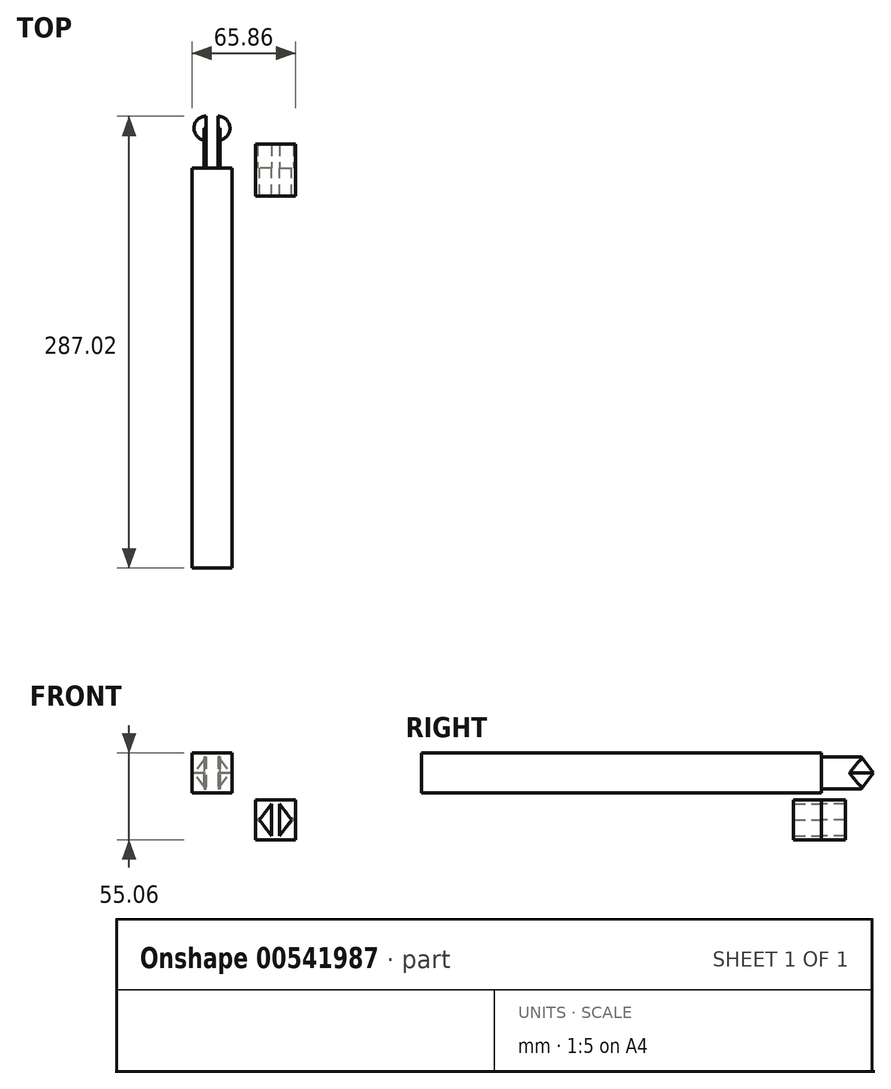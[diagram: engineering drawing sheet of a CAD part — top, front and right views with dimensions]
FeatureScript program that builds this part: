
annotation { "Feature Type Name" : "Feature", "Feature Type Description" : "" }
export const myFeature = defineFeature(function(context is Context, id is Id, definition is map)
    precondition{}
    {
        {
            var Q0;
            Q0=qCreatedBy(makeId("Front.planeOp"),FACE);
            var sketch = newSketch(context, id + "F0", { "sketchPlane" : qUnion([Q0])});
            skLineSegment(sketch, "E0.bottom", {"start": v(-53.16, 42.36) * mm, "end": v(-27.76, 42.36) * mm});
            skLineSegment(sketch, "E0.top", {"start": v(-53.16, 16.96) * mm, "end": v(-27.76, 16.96) * mm});
            skLineSegment(sketch, "E0.left", {"start": v(-53.16, 42.36) * mm, "end": v(-53.16, 16.96) * mm});
            skLineSegment(sketch, "E0.right", {"start": v(-27.76, 42.36) * mm, "end": v(-27.76, 16.96) * mm});
            skSolve(sketch);
        }
        {
            var Q0;
            Q0=makeQuery(id+"F0.imprint","IMPRINT",FACE,{"disambiguationData":[TD([[makeQuery(id+"F0.imprint","IMPRINT",EDGE,{"derivedFrom":sQuery(id+"F0.wireOp",EDGE,"E0.bottom")}),-1.0]])]});
            extrude(context, id + "F1", {"entities" : qUnion([Q0]), "depth" : 254 * mm, "offsetDistance" : 25.4 * mm});
        }
        {
            var Q0;
            Q0=qCreatedBy(makeId("Front.planeOp"),FACE);
            cPlane(context, id + "F2", {"entities" : qUnion([Q0]), "cplaneType" : CPlaneType.OFFSET, "offset" : 25.4 * mm, "oppositeDirection" : true, "width" : 152.4 * mm, "height" : 152.4 * mm});
        }
        {
            var Q0;
            Q0=qCreatedBy(id+"F2.planeOp",FACE);
            var sketch = newSketch(context, id + "F3", { "sketchPlane" : qUnion([Q0])});
            skPoint(sketch, "E1", {"position": v(-36.65, 19.57) * mm});
            skPoint(sketch, "E2", {"position": v(-29.03, 29.73) * mm});
            skPoint(sketch, "E3", {"position": v(-36.65, 39.89) * mm});
            skPoint(sketch, "E4", {"position": v(-44.27, 39.89) * mm});
            skPoint(sketch, "E5", {"position": v(-44.27, 19.57) * mm});
            skPoint(sketch, "E6", {"position": v(-51.9, 29.73) * mm});
            skLineSegment(sketch, "E7", {"start": v(-29.03, 29.73) * mm, "end": v(-36.65, 19.57) * mm});
            skLineSegment(sketch, "E8", {"start": v(-44.27, 19.57) * mm, "end": v(-51.9, 29.73) * mm});
            skLineSegment(sketch, "E9", {"start": v(-44.27, 39.89) * mm, "end": v(-51.9, 29.73) * mm});
            skLineSegment(sketch, "E10", {"start": v(-44.27, 19.57) * mm, "end": v(-44.27, 39.89) * mm});
            skLineSegment(sketch, "E11", {"start": v(-36.65, 39.89) * mm, "end": v(-29.03, 29.73) * mm});
            skLineSegment(sketch, "E12", {"start": v(-36.65, 19.57) * mm, "end": v(-36.65, 39.89) * mm});
            skSolve(sketch);
        }
        {
            var Q0;
            Q0=makeQuery(id+"F1.opExtrude","CAP_FACE",FACE,{"disambiguationData":[OSD([sQuery(id+"F0.wireOp",EDGE,"E0.bottom"),sQuery(id+"F0.wireOp",EDGE,"E0.top"),sQuery(id+"F0.wireOp",EDGE,"E0.left"),sQuery(id+"F0.wireOp",EDGE,"E0.right")])],"isStart":true});
            var sketch = newSketch(context, id + "F4", { "sketchPlane" : qUnion([Q0])});
            skLineSegment(sketch, "E13.bottom", {"start": v(35.38, 39.82) * mm, "end": v(36.65, 39.82) * mm});
            skLineSegment(sketch, "E13.top", {"start": v(35.38, 19.5) * mm, "end": v(36.65, 19.5) * mm});
            skLineSegment(sketch, "E13.left", {"start": v(35.38, 39.82) * mm, "end": v(35.38, 19.5) * mm});
            skLineSegment(sketch, "E13.right", {"start": v(36.65, 39.82) * mm, "end": v(36.65, 19.5) * mm});
            skLineSegment(sketch, "E14", {"start": v(40.46, 42.36) * mm, "end": v(40.46, 16.96) * mm});
            skLineSegment(sketch, "E15.MirrorCS", {"start": v(45.54, 39.82) * mm, "end": v(45.54, 19.5) * mm});
            skLineSegment(sketch, "E16.MirrorCS", {"start": v(45.54, 39.82) * mm, "end": v(44.27, 39.82) * mm});
            skLineSegment(sketch, "E17.MirrorCS", {"start": v(44.27, 39.82) * mm, "end": v(44.27, 19.5) * mm});
            skLineSegment(sketch, "E18.MirrorCS", {"start": v(45.54, 19.5) * mm, "end": v(44.27, 19.5) * mm});
            skSolve(sketch);
        }
        {
            var Q0;
            Q0=makeQuery(id+"F4.imprint","IMPRINT",FACE,{"disambiguationData":[TD([[makeQuery(id+"F4.imprint","IMPRINT",EDGE,{"derivedFrom":sQuery(id+"F4.wireOp",EDGE,"E13.bottom")}),-1.0]])]});
            var Q1;
            Q1=makeQuery(id+"F4.imprint","IMPRINT",FACE,{"disambiguationData":[TD([[makeQuery(id+"F4.imprint","IMPRINT",EDGE,{"derivedFrom":sQuery(id+"F4.wireOp",EDGE,"E15.MirrorCS")}),-1.0]])]});
            extrude(context, id + "F5", {"entities" : qUnion([Q0, Q1]), "operationType" : NewBodyOperationType.ADD, "depth" : 25.4 * mm, "offsetDistance" : 25.4 * mm});
        }
        {
            var Q0;
            Q0=makeQuery(id+"F3.imprint","IMPRINT",FACE,{"disambiguationData":[TD([[makeQuery(id+"F3.imprint","IMPRINT",EDGE,{"derivedFrom":sQuery(id+"F3.wireOp",EDGE,"E8")}),-1.0]])]});
            var Q1;
            Q1=sQuery(id+"F3.wireOp",EDGE,"E10");
            revolve(context, id + "F6", {"operationType" : NewBodyOperationType.ADD, "entities" : qUnion([Q0]), "axis" : qUnion([Q1]), "revolveType" : RevolveType.SYMMETRIC, "angle" : 180 * degree});
        }
        {
            var Q0;
            Q0=makeQuery(id+"F3.imprint","IMPRINT",FACE,{"disambiguationData":[TD([[makeQuery(id+"F3.imprint","IMPRINT",EDGE,{"derivedFrom":sQuery(id+"F3.wireOp",EDGE,"E7")}),-1.0]])]});
            var Q1;
            Q1=sQuery(id+"F3.wireOp",EDGE,"E12");
            revolve(context, id + "F7", {"operationType" : NewBodyOperationType.ADD, "entities" : qUnion([Q0]), "axis" : qUnion([Q1]), "revolveType" : RevolveType.SYMMETRIC, "oppositeDirection" : true, "angle" : 180 * degree});
        }
        {
            var Q0;
            Q0=qCreatedBy(makeId("Front.planeOp"),FACE);
            var sketch = newSketch(context, id + "F8", { "sketchPlane" : qUnion([Q0])});
            skPoint(sketch, "E19", {"position": v(2.54, -10.16) * mm});
            skPoint(sketch, "E20", {"position": v(10.16, 0) * mm});
            skPoint(sketch, "E21", {"position": v(2.54, 10.16) * mm});
            skPoint(sketch, "E22", {"position": v(-2.54, 10.16) * mm});
            skPoint(sketch, "E23", {"position": v(-2.54, -10.16) * mm});
            skPoint(sketch, "E24", {"position": v(-10.16, 0) * mm});
            skLineSegment(sketch, "E25", {"start": v(10.16, 0) * mm, "end": v(2.54, -10.16) * mm});
            skLineSegment(sketch, "E26", {"start": v(-2.54, -10.16) * mm, "end": v(-10.16, 0) * mm});
            skLineSegment(sketch, "E27", {"start": v(-2.54, 10.16) * mm, "end": v(-10.16, 0) * mm});
            skLineSegment(sketch, "E28", {"start": v(-2.54, -10.16) * mm, "end": v(-2.54, 10.16) * mm});
            skLineSegment(sketch, "E29", {"start": v(2.54, 10.16) * mm, "end": v(10.16, 0) * mm});
            skLineSegment(sketch, "E30", {"start": v(2.54, -10.16) * mm, "end": v(2.54, 10.16) * mm});
            skLineSegment(sketch, "E31.bottom", {"start": v(12.7, 12.7) * mm, "end": v(-12.7, 12.7) * mm});
            skLineSegment(sketch, "E31.top", {"start": v(12.7, -12.7) * mm, "end": v(-12.7, -12.7) * mm});
            skLineSegment(sketch, "E31.left", {"start": v(12.7, 12.7) * mm, "end": v(12.7, -12.7) * mm});
            skLineSegment(sketch, "E31.right", {"start": v(-12.7, 12.7) * mm, "end": v(-12.7, -12.7) * mm});
            skSolve(sketch);
        }
        {
            var Q0;
            Q0=makeQuery(id+"F8.imprint","IMPRINT",FACE,{"disambiguationData":[TD([[makeQuery(id+"F8.imprint","IMPRINT",EDGE,{"derivedFrom":sQuery(id+"F8.wireOp",EDGE,"E25")}),1.0]])]});
            extrude(context, id + "F9", {"entities" : qUnion([Q0]), "depth" : 17.78 * mm, "offsetDistance" : 25.4 * mm});
        }
        {
            var Q0;
            Q0=qCreatedBy(makeId("Front.planeOp"),FACE);
            var sketch = newSketch(context, id + "F10", { "sketchPlane" : qUnion([Q0])});
            skPoint(sketch, "E32", {"position": v(2.54, -10.16) * mm});
            skPoint(sketch, "E33", {"position": v(11.38, 0) * mm});
            skPoint(sketch, "E34", {"position": v(2.54, 10.16) * mm});
            skPoint(sketch, "E35", {"position": v(-2.54, 10.16) * mm});
            skPoint(sketch, "E36", {"position": v(-2.54, -10.16) * mm});
            skPoint(sketch, "E37", {"position": v(-11.48, 0) * mm});
            skLineSegment(sketch, "E38", {"start": v(11.38, 0) * mm, "end": v(2.54, -10.16) * mm});
            skLineSegment(sketch, "E39", {"start": v(-2.54, -10.16) * mm, "end": v(-11.48, 0) * mm});
            skLineSegment(sketch, "E40", {"start": v(-2.54, 10.16) * mm, "end": v(-11.48, 0) * mm});
            skLineSegment(sketch, "E41", {"start": v(-2.54, -10.16) * mm, "end": v(-2.54, 10.16) * mm});
            skLineSegment(sketch, "E42", {"start": v(2.54, 10.16) * mm, "end": v(11.38, 0) * mm});
            skLineSegment(sketch, "E43", {"start": v(2.54, -10.16) * mm, "end": v(2.54, 10.16) * mm});
            skLineSegment(sketch, "E44.bottom", {"start": v(12.65, 12.7) * mm, "end": v(-12.75, 12.7) * mm});
            skLineSegment(sketch, "E44.top", {"start": v(12.65, -12.7) * mm, "end": v(-12.75, -12.7) * mm});
            skLineSegment(sketch, "E44.left", {"start": v(12.65, 12.7) * mm, "end": v(12.65, -12.7) * mm});
            skLineSegment(sketch, "E44.right", {"start": v(-12.75, 12.7) * mm, "end": v(-12.75, -12.7) * mm});
            skSolve(sketch);
        }
        {
            var Q0;
            Q0=makeQuery(id+"F10.imprint","IMPRINT",FACE,{"disambiguationData":[TD([[makeQuery(id+"F10.imprint","IMPRINT",EDGE,{"derivedFrom":sQuery(id+"F10.wireOp",EDGE,"E38")}),1.0]])]});
            extrude(context, id + "F11", {"entities" : qUnion([Q0]), "operationType" : NewBodyOperationType.ADD, "oppositeDirection" : true, "depth" : 15.24 * mm, "offsetDistance" : 25.4 * mm});
        }
    });
